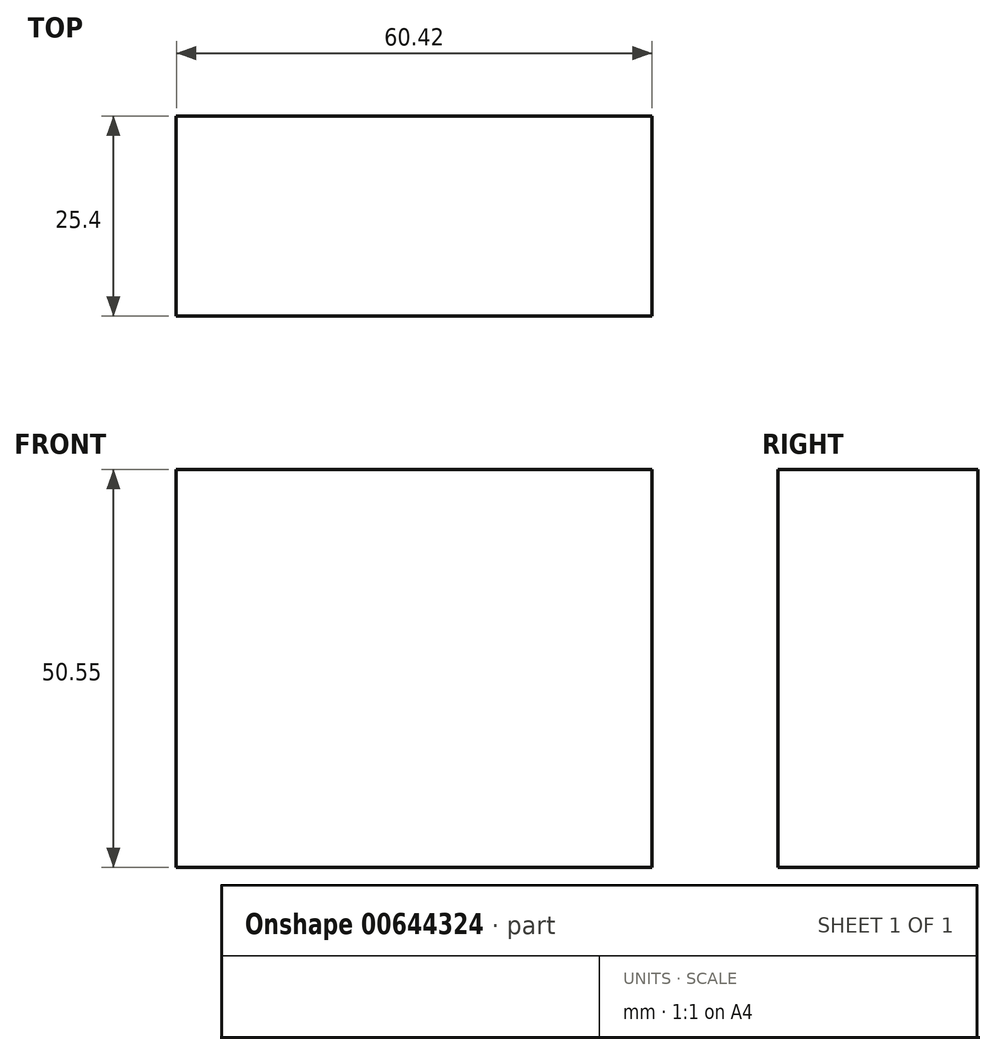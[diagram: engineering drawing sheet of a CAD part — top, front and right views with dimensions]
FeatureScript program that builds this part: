
annotation { "Feature Type Name" : "Feature", "Feature Type Description" : "" }
export const myFeature = defineFeature(function(context is Context, id is Id, definition is map)
    precondition{}
    {
        {
            var Q0;
            Q0=qCreatedBy(makeId("Front.planeOp"),FACE);
            var sketch = newSketch(context, id + "F0", { "sketchPlane" : qUnion([Q0])});
            skLineSegment(sketch, "E0.bottom", {"start": v(-18.21, 33.94) * mm, "end": v(42.21, 33.94) * mm});
            skLineSegment(sketch, "E0.top", {"start": v(-18.21, -16.61) * mm, "end": v(42.21, -16.61) * mm});
            skLineSegment(sketch, "E0.left", {"start": v(-18.21, 33.94) * mm, "end": v(-18.21, -16.61) * mm});
            skLineSegment(sketch, "E0.right", {"start": v(42.21, 33.94) * mm, "end": v(42.21, -16.61) * mm});
            skSolve(sketch);
        }
        {
            var Q0;
            Q0=makeQuery(id+"F0.imprint","IMPRINT",FACE,{"disambiguationData":[TD([[makeQuery(id+"F0.imprint","IMPRINT",EDGE,{"derivedFrom":sQuery(id+"F0.wireOp",EDGE,"E0.bottom")}),-1.0]])]});
            extrude(context, id + "F1", {"entities" : qUnion([Q0]), "depth" : 25.4 * mm, "offsetDistance" : 25.4 * mm});
        }
    });
